# Revit family: Hager-Univers-IP55-D275-H800-Cl.II-Steel_encl-ES-es
name_source: partatom
category: Equipement électrique
units: mm (PartAtom-declared; Revit-internal decimal feet)

## family parameters
Configuration du panneau = Deux colonnes, circuits au sein
Cote de connecteur circulaire = Utiliser le diamètre
Couper avec des vides une fois chargée = Non
Hôte = Face
Partagée = Non
Point de calcul de pièce = Non
Type d'élément = Tableau de raccordement

## types (5) — shared parameters
Commentaires du type = Univers
EF000003 - Tipo de montaje = EV000384 - Montado superficial (escayola)
EF000007 - Color = EV000270 - Gris
EF000040 - Altura = 800 mm  [stored 2.62467 ft]
EF000049 - Profundidad = 275 mm
EF000116 - Número RAL = 7035
EF000118 - Con placa de montaje = Non
EF000266 - Número de filas = 5
EF000339 - Tipo de cubierta = EV004216 - Puerta
EF001088 - Posibilidad de extensión = Oui
EF001131 - Profundidad interna = 275 mm
EF001596 - Material de la carcasa = EV000179 - Acero
EF001613 - Integridad del circuito = EV000494 - Ninguno
EF002950 - Anchura de unidades de división = 24
EF003532 - Adecuado para uso en exteriores = Non
EF004293 - Resistencia al impacto (IK) = EV008784 - IK10
EF005474 - Grado de protección (IP) = EV006420 - IP55
EF006244 - Tapa/puerta transparente = Non
EF006306 - Con cierre = Non
EF007800 - Adecuado para la protección contra rayos = Non
EF008873 - Corriente nominal (In) = 800 A
EF009170 - Espesor del material de la caja = 2 mm  [stored 0.00656168 ft]
EF009171 - Espesor puerta/tapa = 2 mm  [stored 0.00656168 ft]
EF009212 - Versión de la cubierta = EV000116 - Cerrado
EF015940 - Tapa con alivio de sobrepresión = Non
Fabricant = Hager
HG000002 - Con puerta o tapa = Oui
HG000003 - Gama = Univers
HG000006 - Empotrado = Non
HG000023 - Caja de doble sección = Non
HG000024 - Altura de la sección inferior = 800 mm  [stored 2.62467 ft]
HG000026 - Instalación en suelo = Non
zero-valued in all types: EF000218 - Profundidad de instalación, Elévation par défaut, HG000027 - Altura de zócalo

## per-type parameters (varying)
| type | EF000008 - Anchura | EF000437 - Número de entradas de conductos de cables | EF004427 - Número de módulos | EF004464 - Tipo de puerta | EF009554 - Número de aberturas para placas-brida | HG000004 - Referencia del fabricante | HG000009 - Puerta batiente doble | HG000010 - Puertas asimétricas |
| Montado superficial (escayola) IP55 A1050 A800 P275  - FR54S | 1050 mm | 8 | 240 | EV003602 - Doble | 8 | FR54S | Oui | Non |
| Montado superficial (escayola) IP55 A1300 A800 P275  - FR55S | 1300 mm  [stored 4.26509 ft] | 10 | 300 | EV003602 - Doble | 10 | FR55S | Oui | Oui |
| Montado superficial (escayola) IP55 A300 A800 P275  - FR51S | 300 mm | 2 | 60 | EV002646 - Único | 2 | FR51S | Non | Non |
| Montado superficial (escayola) IP55 A550 A800 P275  - FR52S | 550 mm | 4 | 120 | EV002646 - Único | 4 | FR52S | Non | Non |
| Montado superficial (escayola) IP55 A800 A800 P275  - FR53S | 800 mm  [stored 2.62467 ft] | 6 | 180 | EV002646 - Único | 6 | FR53S | Non | Non |

note: [stored X ft] marks values corroborated as IEEE doubles in the binary element streams (Revit-internal decimal feet)

## geometry (parser evidence)
native form markers: Sweep x10
no freeform markers — native parametric forms only
